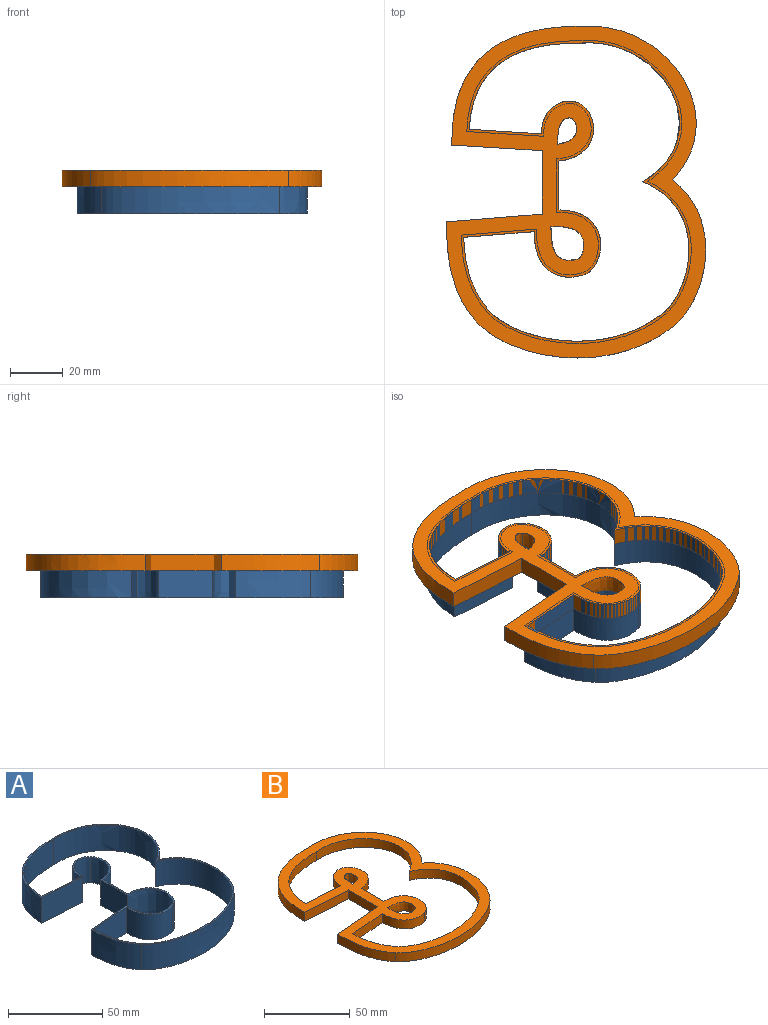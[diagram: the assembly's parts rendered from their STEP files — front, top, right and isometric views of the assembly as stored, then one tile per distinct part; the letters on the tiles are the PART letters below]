
ASSEMBLY  parts=2 mates=1
PART A: 26 faces, bbox 94.4x122.5x20.9 mm
  f0: plane 122.53x94.38mm, normal (0,0,1), area 443.1mm2, adj f2,f3,f4,f5,f6,f7,f8,f9
  f1: plane 122.53x94.38mm, normal (0,0,-1), area 443.1mm2, adj f2,f3,f4,f5,f6,f7,f8,f9
  f2: plane 29.01x16.51mm, normal (-0.06,-1,0), area 479.9mm2, adj f0,f1,f3,f13
  f3: extruded ~16.51x15.45mm, area 398.6mm2, adj f0,f1,f2,f4
  f4: extruded ~18.33x16.51mm, area 443.5mm2, adj f0,f1,f3,f5
  f5: plane 20.16x16.51mm, normal (-1,0,0), area 332.8mm2, adj f0,f1,f4,f6
  f6: extruded ~22.9x16.51mm, area 591.7mm2, adj f0,f1,f5,f7
  f7: extruded ~17.32x17.18mm, area 478.7mm2, adj f0,f1,f6,f8
  f8: plane 28.46x16.51mm, normal (-0.08,1,0), area 471.4mm2, adj f0,f1,f7,f9
  f9: extruded ~28.53x16.51mm, area 505.6mm2, adj f0,f1,f8,f10
  f10: extruded ~67.23x16.51mm, area 1200.5mm2, adj f0,f1,f9,f11
  f11: extruded ~50.84x16.51mm, area 998.1mm2, adj f0,f1,f10,f12
  f12: extruded ~53.37x38.98mm, area 1360.4mm2, adj f0,f1,f11,f13
  f13: extruded ~42.4x34.34mm, area 1024.1mm2, adj f0,f1,f2,f12
  f14: plane 27.23x16.51mm, normal (0.06,1,0), area 450.4mm2, adj f0,f1,f15,f25
  f15: extruded ~16.97x16.51mm, area 418.2mm2, adj f0,f1,f14,f16
  f16: extruded ~19.72x16.51mm, area 462.7mm2, adj f0,f1,f15,f17
  f17: plane 18.48x16.51mm, normal (1,0,0), area 305.2mm2, adj f0,f1,f16,f18
  f18: extruded ~24.64x16.51mm, area 619.5mm2, adj f0,f1,f17,f19
  f19: extruded ~18.3x17.25mm, area 489.9mm2, adj f0,f1,f18,f20
  f20: plane 26.65x16.51mm, normal (0.08,-1,0), area 441.5mm2, adj f0,f1,f19,f21
  f21: extruded ~27.14x16.51mm, area 482mm2, adj f0,f1,f20,f22
  f22: extruded ~66x16.51mm, area 1178mm2, adj f0,f1,f21,f23
  f23: extruded ~49.98x17.47mm, area 995.5mm2, adj f0,f1,f22,f24
  f24: extruded ~52.64x38.04mm, area 1349.8mm2, adj f0,f1,f23,f25
  f25: extruded ~41.5x32.62mm, area 988mm2, adj f0,f1,f14,f24
PART B: 26 faces, bbox 103.2x130.7x11.4 mm
  f0: plane 130.71x103.2mm, normal (0,0,1), area 3270.4mm2, adj f2,f3,f4,f5,f6,f7,f8,f9
  f1: plane 130.71x103.2mm, normal (0,0,-1), area 3270.4mm2, adj f2,f3,f4,f5,f6,f7,f8,f9
  f2: plane 34.24x6.35mm, normal (-0.06,-1,0), area 217.8mm2, adj f0,f1,f5,f13
  f3: extruded ~9.97x6.35mm, area 86.8mm2, adj f0,f1,f4
  f4: extruded ~9.17x7.26mm, area 87.6mm2, adj f0,f1,f3
  f5: plane 24.01x6.35mm, normal (-1,0,0), area 152.5mm2, adj f0,f1,f2,f8
  f6: extruded ~12.5x12.04mm, area 137.5mm2, adj f0,f1,f7
  f7: extruded ~12.8x10.7mm, area 129.3mm2, adj f0,f1,f6
  f8: plane 36.24x6.35mm, normal (-0.08,1,0), area 230.8mm2, adj f0,f1,f5,f9
  f9: extruded ~37.05x10.76mm, area 251mm2, adj f0,f1,f8,f10
  f10: extruded ~74.78x14.43mm, area 515.1mm2, adj f0,f1,f9,f11
  f11: extruded ~55.83x12.6mm, area 402.1mm2, adj f0,f1,f10,f12
  f12: extruded ~58.15x44.65mm, area 560.8mm2, adj f0,f1,f11,f13
  f13: extruded ~47.89x44.92mm, area 479.5mm2, adj f0,f1,f2,f12
  f14: plane 27.23x6.35mm, normal (0.06,1,0), area 173.2mm2, adj f0,f1,f15,f25
  f15: extruded ~16.97x12.34mm, area 160.9mm2, adj f0,f1,f14,f16
  f16: extruded ~19.72x13.09mm, area 178mm2, adj f0,f1,f15,f17
  f17: plane 18.48x6.35mm, normal (1,0,0), area 117.4mm2, adj f0,f1,f16,f18
  f18: extruded ~24.64x15.83mm, area 238.3mm2, adj f0,f1,f17,f19
  f19: extruded ~18.3x17.25mm, area 188.4mm2, adj f0,f1,f18,f20
  f20: plane 26.65x6.35mm, normal (0.08,-1,0), area 169.8mm2, adj f0,f1,f19,f21
  f21: extruded ~27.14x9.07mm, area 185.4mm2, adj f0,f1,f20,f22
  f22: extruded ~66x12.15mm, area 453.1mm2, adj f0,f1,f21,f23
  f23: extruded ~49.98x17.47mm, area 382.9mm2, adj f0,f1,f22,f24
  f24: extruded ~52.64x38.04mm, area 519.1mm2, adj f0,f1,f23,f25
  f25: extruded ~41.5x32.62mm, area 380mm2, adj f0,f1,f14,f24
PLACE A t=(41.63,45.65,27.15)mm
PLACE B t=(-56.12,29.15,37.31)mm
MATE fastened A.f0 <-> B.f0  axis (0,0,1) through (58.31,48.65,43.66)mm
